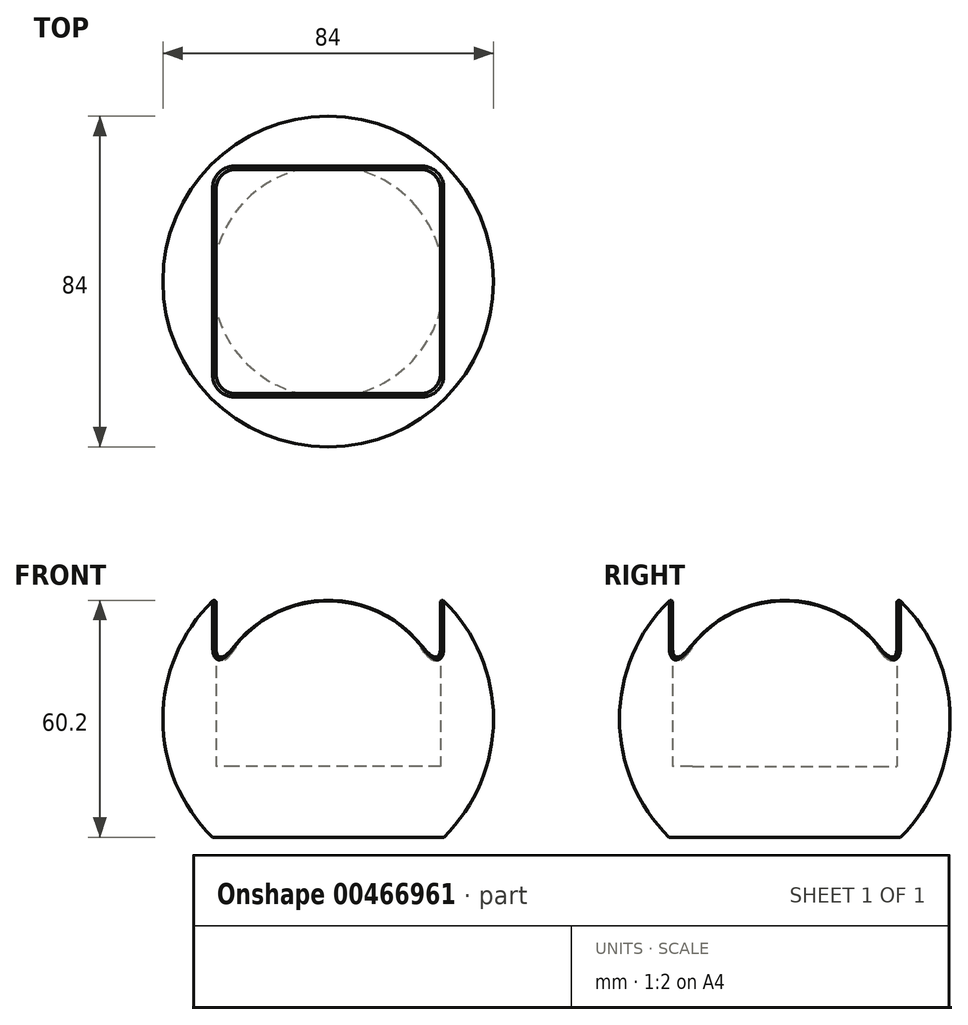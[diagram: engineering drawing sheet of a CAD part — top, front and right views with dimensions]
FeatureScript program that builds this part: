
annotation { "Feature Type Name" : "Feature", "Feature Type Description" : "" }
export const myFeature = defineFeature(function(context is Context, id is Id, definition is map)
    precondition{}
    {
        {
            var Q0;
            Q0=qCreatedBy(makeId("Top.planeOp"),FACE);
            var sketch = newSketch(context, id + "F0", { "sketchPlane" : qUnion([Q0])});
            skLineSegment(sketch, "E0.bottom", {"start": v(23.5, -28.5) * mm, "end": v(-23.5, -28.5) * mm});
            skLineSegment(sketch, "E0.top", {"start": v(23.5, 28.5) * mm, "end": v(-23.5, 28.5) * mm});
            skLineSegment(sketch, "E0.left", {"start": v(28.5, -23.5) * mm, "end": v(28.5, 23.5) * mm});
            skLineSegment(sketch, "E0.right", {"start": v(-28.5, -23.5) * mm, "end": v(-28.5, 23.5) * mm});
            skPoint(sketch, "E0.middle", {"position": v(0, 0) * mm});
            skPoint(sketch, "E1.visualSharp", {"position": v(-28.5, 28.5) * mm});
            skArc(sketch, "E1.filletArc", {"start": v(-23.5, 28.5) * mm, "mid": v(-27.04, 27.04) * mm, "end": v(-28.5, 23.5) * mm});
            skPoint(sketch, "E2.visualSharp", {"position": v(28.5, 28.5) * mm});
            skArc(sketch, "E2.filletArc", {"start": v(28.5, 23.5) * mm, "mid": v(27.04, 27.04) * mm, "end": v(23.5, 28.5) * mm});
            skPoint(sketch, "E3.visualSharp", {"position": v(28.5, -28.5) * mm});
            skArc(sketch, "E3.filletArc", {"start": v(23.5, -28.5) * mm, "mid": v(27.04, -27.04) * mm, "end": v(28.5, -23.5) * mm});
            skPoint(sketch, "E4.visualSharp", {"position": v(-28.5, -28.5) * mm});
            skArc(sketch, "E4.filletArc", {"start": v(-28.5, -23.5) * mm, "mid": v(-27.04, -27.04) * mm, "end": v(-23.5, -28.5) * mm});
            skArc(sketch, "E5", {"start": v(42, 0) * mm, "mid": v(0, 42) * mm, "end": v(-42, 0) * mm});
            skLineSegment(sketch, "E6", {"start": v(-42, 0) * mm, "end": v(42, 0) * mm, "construction": true});
            skSolve(sketch);
        }
        {
            var Q0;
            Q0=makeQuery(id+"F0.imprint","IMPRINT",FACE,{"disambiguationData":[TD([[makeQuery(id+"F0.imprint","IMPRINT",EDGE,{"derivedFrom":sQuery(id+"F0.wireOp",EDGE,"E0.bottom")}),-1.0]])]});
            extrude(context, id + "F1", {"entities" : qUnion([Q0]), "depth" : 100 * mm});
        }
        {
            var Q0;
            Q0=qCreatedBy(makeId("Front.planeOp"),FACE);
            var sketch = newSketch(context, id + "F2", { "sketchPlane" : qUnion([Q0])});
            skArc(sketch, "E7", {"start": v(0, -30) * mm, "mid": v(42, 12) * mm, "end": v(0, 54) * mm});
            skLineSegment(sketch, "E8", {"start": v(29.4, -18) * mm, "end": v(0, -18) * mm});
            skLineSegment(sketch, "E9", {"start": v(0, -18) * mm, "end": v(0, 54) * mm});
            skPoint(sketch, "E10", {"position": v(29.02, 42.36) * mm});
            skSolve(sketch);
        }
        {
            var Q0;
            {var subQ2=sQuery(id+"F2.wireOp",EDGE,"E8");Q0=makeQuery(id+"F2.imprint","IMPRINT",FACE,{"disambiguationData":[TD([[makeQuery(id+"F2.imprint","IMPRINT",EDGE,{"derivedFrom":subQ2}),-1.0]])]});}
            var Q1;
            Q1=sQuery(id+"F2.wireOp",EDGE,"E9");
            revolve(context, id + "F3", {"entities" : qUnion([Q0]), "axis" : qUnion([Q1]), "revolveType" : RevolveType.FULL});
        }
        {
            var Q0;
            Q0=makeQuery(id+"F1.opExtrude","SWEPT_BODY",BODY,{"disambiguationData":[OSD([sQuery(id+"F0.wireOp",EDGE,"E0.bottom"),sQuery(id+"F0.wireOp",EDGE,"E0.top"),sQuery(id+"F0.wireOp",EDGE,"E0.left"),sQuery(id+"F0.wireOp",EDGE,"E0.right"),sQuery(id+"F0.wireOp",EDGE,"E1.filletArc"),sQuery(id+"F0.wireOp",EDGE,"E2.filletArc"),sQuery(id+"F0.wireOp",EDGE,"E3.filletArc"),sQuery(id+"F0.wireOp",EDGE,"E4.filletArc")])]});
            var Q1;
            Q1=makeQuery(id+"F3.opRevolve","SWEPT_BODY",BODY,{"disambiguationData":[OSD([sQuery(id+"F2.wireOp",EDGE,"E7"),sQuery(id+"F2.wireOp",EDGE,"E8"),sQuery(id+"F2.wireOp",EDGE,"E9")])]});
            booleanBodies(context, id + "F4", {"operationType" : BooleanOperationType.SUBTRACTION, "tools" : qUnion([Q0]), "targets" : qUnion([Q1])});
        }
        {
            var Q0;
            Q0=makeQuery(id+"F4.opBoolean","INTERSECT",EDGE,{"derivedFrom":[makeQuery(id+"F1.opExtrude","SWEPT_FACE",FACE,{"disambiguationData":[OSD([sQuery(id+"F0.wireOp",EDGE,"E0.bottom")])]}),makeQuery(id+"F3.opRevolve","SWEPT_FACE",FACE,{"disambiguationData":[OSD([sQuery(id+"F2.wireOp",EDGE,"E7")])]})]});
            var Q1;
            Q1=makeQuery(id+"F4.opBoolean","INTERSECT",EDGE,{"derivedFrom":[makeQuery(id+"F1.opExtrude","SWEPT_FACE",FACE,{"disambiguationData":[OSD([sQuery(id+"F0.wireOp",EDGE,"E4.filletArc")])]}),makeQuery(id+"F3.opRevolve","SWEPT_FACE",FACE,{"disambiguationData":[OSD([sQuery(id+"F2.wireOp",EDGE,"E7")])]})]});
            var Q2;
            Q2=makeQuery(id+"F4.opBoolean","INTERSECT",EDGE,{"derivedFrom":[makeQuery(id+"F1.opExtrude","SWEPT_FACE",FACE,{"disambiguationData":[OSD([sQuery(id+"F0.wireOp",EDGE,"E0.right")])]}),makeQuery(id+"F3.opRevolve","SWEPT_FACE",FACE,{"disambiguationData":[OSD([sQuery(id+"F2.wireOp",EDGE,"E7")])]})]});
            var Q3;
            Q3=makeQuery(id+"F4.opBoolean","INTERSECT",EDGE,{"derivedFrom":[makeQuery(id+"F1.opExtrude","SWEPT_FACE",FACE,{"disambiguationData":[OSD([sQuery(id+"F0.wireOp",EDGE,"E1.filletArc")])]}),makeQuery(id+"F3.opRevolve","SWEPT_FACE",FACE,{"disambiguationData":[OSD([sQuery(id+"F2.wireOp",EDGE,"E7")])]})]});
            var Q4;
            Q4=makeQuery(id+"F4.opBoolean","INTERSECT",EDGE,{"derivedFrom":[makeQuery(id+"F1.opExtrude","SWEPT_FACE",FACE,{"disambiguationData":[OSD([sQuery(id+"F0.wireOp",EDGE,"E0.top")])]}),makeQuery(id+"F3.opRevolve","SWEPT_FACE",FACE,{"disambiguationData":[OSD([sQuery(id+"F2.wireOp",EDGE,"E7")])]})]});
            var Q5;
            Q5=makeQuery(id+"F4.opBoolean","INTERSECT",EDGE,{"derivedFrom":[makeQuery(id+"F1.opExtrude","SWEPT_FACE",FACE,{"disambiguationData":[OSD([sQuery(id+"F0.wireOp",EDGE,"E2.filletArc")])]}),makeQuery(id+"F3.opRevolve","SWEPT_FACE",FACE,{"disambiguationData":[OSD([sQuery(id+"F2.wireOp",EDGE,"E7")])]})]});
            var Q6;
            Q6=makeQuery(id+"F4.opBoolean","INTERSECT",EDGE,{"derivedFrom":[makeQuery(id+"F1.opExtrude","SWEPT_FACE",FACE,{"disambiguationData":[OSD([sQuery(id+"F0.wireOp",EDGE,"E0.left")])]}),makeQuery(id+"F3.opRevolve","SWEPT_FACE",FACE,{"disambiguationData":[OSD([sQuery(id+"F2.wireOp",EDGE,"E7")])]})]});
            var Q7;
            Q7=makeQuery(id+"F4.opBoolean","INTERSECT",EDGE,{"derivedFrom":[makeQuery(id+"F1.opExtrude","SWEPT_FACE",FACE,{"disambiguationData":[OSD([sQuery(id+"F0.wireOp",EDGE,"E3.filletArc")])]}),makeQuery(id+"F3.opRevolve","SWEPT_FACE",FACE,{"disambiguationData":[OSD([sQuery(id+"F2.wireOp",EDGE,"E7")])]})]});
            fillet(context, id + "F5", {"entities" : qUnion([Q0, Q1, Q2, Q3, Q4, Q5, Q6, Q7]), "radius" : 0.5 * mm, "tangentPropagation" : true, "rho" : 0.3, "crossSection" : FilletCrossSection.CONIC, "allowEdgeOverflow" : false});
        }
    });
